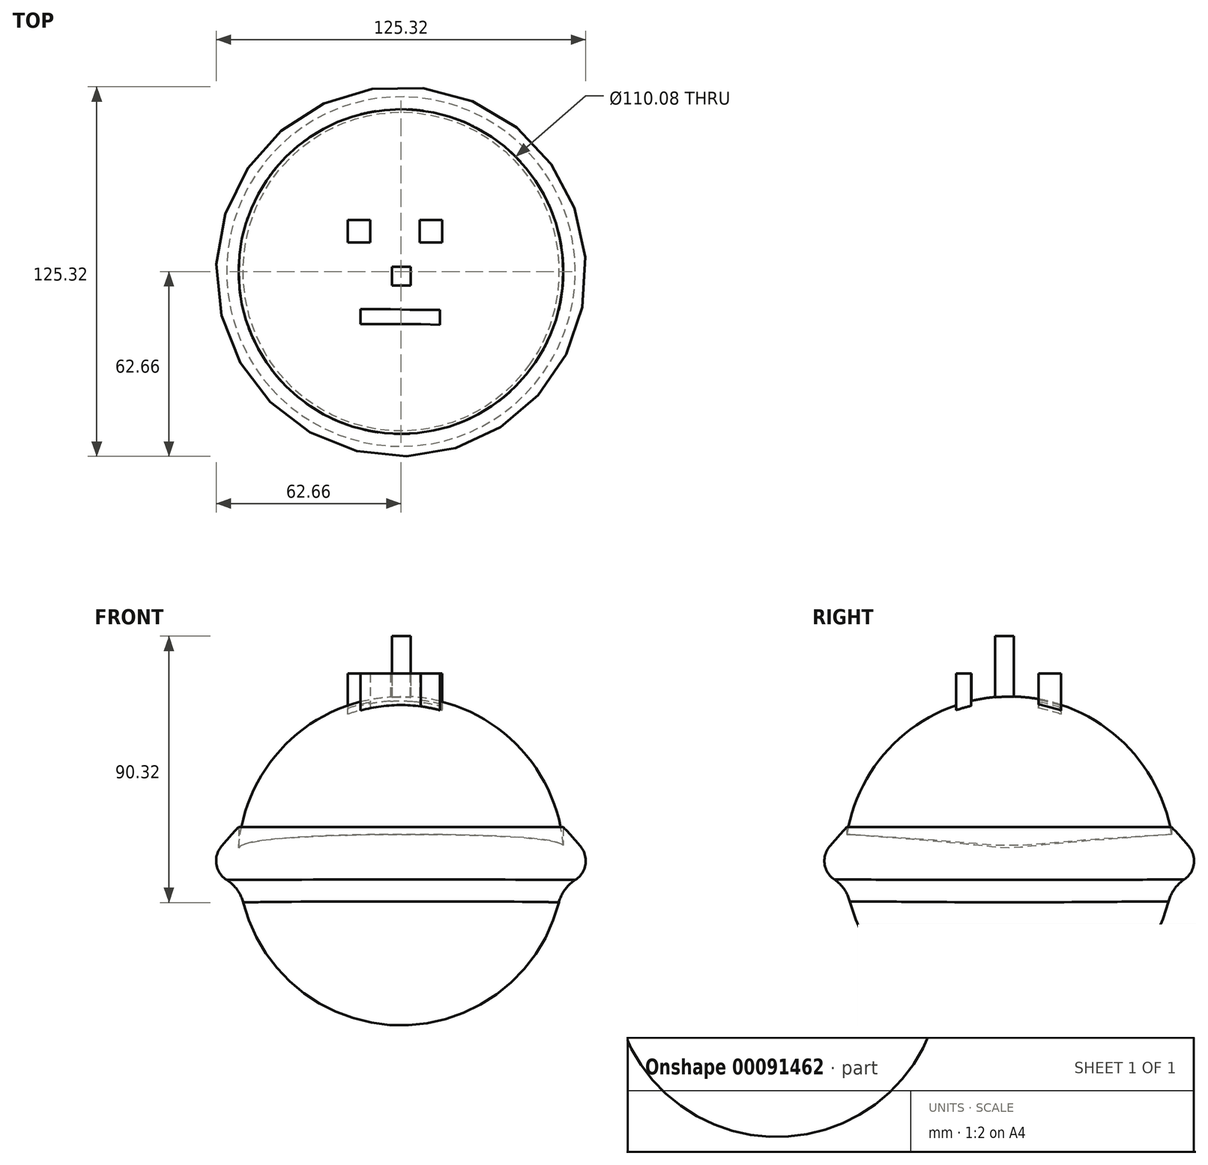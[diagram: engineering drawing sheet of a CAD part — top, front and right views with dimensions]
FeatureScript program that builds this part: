
annotation { "Feature Type Name" : "Feature", "Feature Type Description" : "" }
export const myFeature = defineFeature(function(context is Context, id is Id, definition is map)
    precondition{}
    {
        {
            var Q0;
            Q0=qCreatedBy(makeId("Front.planeOp"),FACE);
            var sketch = newSketch(context, id + "F0", { "sketchPlane" : qUnion([Q0])});
            skLineSegment(sketch, "E0", {"start": v(0, 0) * mm, "end": v(69.85, 0) * mm});
            skArc(sketch, "E1", {"start": v(69.85, 0) * mm, "mid": v(39.9, 32.25) * mm, "end": v(0, 50.8) * mm});
            skLineSegment(sketch, "E2", {"start": v(0, 50.8) * mm, "end": v(0, 0) * mm});
            skSolve(sketch);
        }
        {
            var Q0;
            Q0=makeQuery(id+"F0.imprint","IMPRINT",FACE,{"disambiguationData":[TD([[makeQuery(id+"F0.imprint","IMPRINT",EDGE,{"derivedFrom":sQuery(id+"F0.wireOp",EDGE,"E0")}),1.0]])]});
            var Q1;
            Q1=sQuery(id+"F0.wireOp",EDGE,"E2");
            revolve(context, id + "F1", {"entities" : qUnion([Q0]), "axis" : qUnion([Q1]), "revolveType" : RevolveType.FULL});
        }
        {
            var Q0;
            Q0=makeQuery(id+"F1.opRevolve","SWEPT_FACE",FACE,{"disambiguationData":[OSD([sQuery(id+"F0.wireOp",EDGE,"E1")])]});
            fillet(context, id + "F2", {"entities" : qUnion([Q0]), "radius" : 7.62 * mm, "tangentPropagation" : true, "allowEdgeOverflow" : false});
        }
        {
            var Q0;
            Q0=makeQuery(id+"F1.opRevolve","SWEPT_FACE",FACE,{"disambiguationData":[OSD([sQuery(id+"F0.wireOp",EDGE,"E0")])]});
            extrude(context, id + "F3", {"entities" : qUnion([Q0]), "operationType" : NewBodyOperationType.REMOVE, "oppositeDirection" : true, "depth" : 25.4 * mm});
        }
        {
            var Q0;
            Q0=qCreatedBy(makeId("Top.planeOp"),FACE);
            cPlane(context, id + "F4", {"entities" : qUnion([Q0]), "cplaneType" : CPlaneType.OFFSET, "offset" : 7.62 * mm, "width" : 152.4 * mm, "height" : 152.4 * mm});
        }
        {
            var Q0;
            Q0=qCreatedBy(id+"F4.planeOp",FACE);
            var sketch = newSketch(context, id + "F5", { "sketchPlane" : qUnion([Q0])});
            skLineSegment(sketch, "E3", {"start": v(0, 0) * mm, "end": v(76.56, 0) * mm});
            skLineSegment(sketch, "E4", {"start": v(0, 0) * mm, "end": v(-76.56, 0) * mm});
            skLineSegment(sketch, "E5", {"start": v(56.38, 0) * mm, "end": v(-57.92, 0) * mm});
            skArc(sketch, "E6", {"start": v(-55.17, 0) * mm, "mid": v(0.03, -55.77) * mm, "end": v(55.23, 0) * mm});
            skSolve(sketch);
        }
        {
            var Q0;
            Q0 = qSketchRegion(id + "F5", true);
            var Q1;
            Q1=sQuery(id+"F5.wireOp",EDGE,"E4");
            revolve(context, id + "F6", {"operationType" : NewBodyOperationType.ADD, "entities" : qUnion([Q0]), "axis" : qUnion([Q1]), "revolveType" : RevolveType.FULL});
        }
        {
            var Q0;
            Q0=qCreatedBy(makeId("Top.planeOp"),FACE);
            cPlane(context, id + "F7", {"entities" : qUnion([Q0]), "cplaneType" : CPlaneType.OFFSET, "offset" : 45.72 * mm, "width" : 152.4 * mm, "height" : 152.4 * mm});
        }
        {
            var Q0;
            Q0=qCreatedBy(id+"F7.planeOp",FACE);
            var sketch = newSketch(context, id + "F8", { "sketchPlane" : qUnion([Q0])});
            skLineSegment(sketch, "E7.bottom", {"start": v(-3.03, 1.6) * mm, "end": v(3.32, 1.6) * mm});
            skLineSegment(sketch, "E7.top", {"start": v(-3.03, -4.75) * mm, "end": v(3.32, -4.75) * mm});
            skLineSegment(sketch, "E7.left", {"start": v(-3.03, 1.6) * mm, "end": v(-3.03, -4.75) * mm});
            skLineSegment(sketch, "E7.right", {"start": v(3.32, 1.6) * mm, "end": v(3.32, -4.75) * mm});
            skSolve(sketch);
        }
        {
            var Q0;
            Q0 = qSketchRegion(id + "F8", true);
            extrude(context, id + "F9", {"entities" : qUnion([Q0]), "operationType" : NewBodyOperationType.ADD, "depth" : 38.1 * mm});
        }
        {
            var Q0;
            Q0=qCreatedBy(id+"F7.planeOp",FACE);
            var sketch = newSketch(context, id + "F10", { "sketchPlane" : qUnion([Q0])});
            skLineSegment(sketch, "E8", {"start": v(-18.02, 17.54) * mm, "end": v(-18.02, 9.92) * mm});
            skLineSegment(sketch, "E9", {"start": v(-18.02, 9.92) * mm, "end": v(-10.4, 9.92) * mm});
            skLineSegment(sketch, "E10", {"start": v(-10.4, 9.92) * mm, "end": v(-10.4, 17.54) * mm});
            skLineSegment(sketch, "E11", {"start": v(-10.4, 17.54) * mm, "end": v(-18.02, 17.54) * mm});
            skLineSegment(sketch, "E12", {"start": v(6.42, 9.92) * mm, "end": v(6.42, 17.54) * mm});
            skPoint(sketch, "E12.endSnap0", {"position": v(-14.2, 17.54) * mm});
            skLineSegment(sketch, "E13", {"start": v(6.42, 17.54) * mm, "end": v(14.04, 17.54) * mm});
            skLineSegment(sketch, "E14", {"start": v(14.04, 17.54) * mm, "end": v(14.04, 9.92) * mm});
            skLineSegment(sketch, "E15", {"start": v(14.04, 9.92) * mm, "end": v(6.42, 9.92) * mm});
            skSolve(sketch);
        }
        {
            var Q0;
            Q0 = qSketchRegion(id + "F10", true);
            extrude(context, id + "F11", {"entities" : qUnion([Q0]), "operationType" : NewBodyOperationType.ADD, "depth" : 25.4 * mm});
        }
        {
            var Q0;
            Q0=qCreatedBy(id+"F7.planeOp",FACE);
            var sketch = newSketch(context, id + "F12", { "sketchPlane" : qUnion([Q0])});
            skLineSegment(sketch, "E16", {"start": v(-3.56, -12.75) * mm, "end": v(-13.72, -12.75) * mm});
            skLineSegment(sketch, "E17", {"start": v(-13.72, -12.75) * mm, "end": v(-13.72, -17.83) * mm});
            skLineSegment(sketch, "E18", {"start": v(-13.72, -17.83) * mm, "end": v(0, -17.83) * mm});
            skLineSegment(sketch, "E19", {"start": v(0, -17.83) * mm, "end": v(6.75, -17.83) * mm});
            skLineSegment(sketch, "E20", {"start": v(-3.56, -12.75) * mm, "end": v(3.07, -12.93) * mm});
            skLineSegment(sketch, "E21", {"start": v(3.07, -12.93) * mm, "end": v(13.23, -12.93) * mm});
            skLineSegment(sketch, "E22", {"start": v(13.23, -12.93) * mm, "end": v(13.23, -18.01) * mm});
            skLineSegment(sketch, "E23", {"start": v(13.23, -18.01) * mm, "end": v(6.75, -17.83) * mm});
            skSolve(sketch);
        }
        {
            var Q0;
            Q0 = qSketchRegion(id + "F12", true);
            extrude(context, id + "F13", {"entities" : qUnion([Q0]), "operationType" : NewBodyOperationType.ADD, "depth" : 25.4 * mm});
        }
        {
            var Q0;
            {var subQ0=sQuery(id+"F0.wireOp",EDGE,"E1");var subQ1=sQuery(id+"F0.wireOp",EDGE,"E0");Q0=makeQuery(id+"F6.boolean.opBoolean","SPLIT",FACE,{"disambiguationData":[TD([makeQuery(id+"F2.opFillet","BLEND_FACE",FACE,{"disambiguationData":[OSD([subQ1,subQ0])]}),makeQuery(id+"F3.boolean.opBoolean","COPY",FACE,{"derivedFrom":makeQuery(id+"F3.opExtrude","SWEPT_FACE",FACE,{"disambiguationData":[OSD([subQ1,subQ0])]})})])],"derivedFrom":makeQuery(id+"F6.opRevolve","SWEPT_FACE",FACE,{"disambiguationData":[OSD([sQuery(id+"F5.wireOp",EDGE,"E6")])]})});}
            fillet(context, id + "F14", {"entities" : qUnion([Q0]), "radius" : 12.7 * mm, "tangentPropagation" : true, "allowEdgeOverflow" : false});
        }
    });
